# Revit family: TR3106
name_source: partatom
category: Verbindungsmittel
units: mm (PartAtom-declared; Revit-internal decimal feet)

## family parameters
Arbeitsebenenbasiert = Nein
Beim Laden mit Abzugskörper schneiden = Nein
Gemeinsam genutzt = Nein
Immer vertikal = Nein
OmniClass-Nummer = 23.25.10.27.11.21
OmniClass-Titel = Reinforcement Couplers

## types (9) — shared parameters
Endenbearbeitung 1 = Mit Gewinde
Endenbearbeitung 2 = Mit Gewinde
Hersteller = Stahlwerk Annahütte Max Aicher GmbH Co.KG
Körper = 0,00 kg
Modell = TR 3106
TR3106-L_Vis = Ja
TR3106_Vis = Ja
Typenbild = TR3106.png
URL = http//:www.annahuette.com

## per-type parameters (varying)
| type | Außendurchmesser | Beschreibung | Einfassung Stab 1 | Einfassung Stab 2 | Gesamtlänge | Stabgröße 1 | Stabgröße 2 | TR3106-L | TR3106-L0 | TR3106-L1 | TR3106-L2 | TR3106-Stab1 | TR3106-Stab2 | TR3106-ød | Typenkommentare |
| TR 3106-ø22/18 | 32 mm  [stored 0.104987 ft] | TR3106-ø22/18 | 35 mm  [stored 0.114829 ft] | 35 mm  [stored 0.114829 ft] | 90 mm  [stored 0.295276 ft] | SAS 670 - ø22 | SAS 670 - ø18 | 90 mm  [stored 0.295276 ft] | 45 mm  [stored 0.147638 ft] | 35 mm  [stored 0.114829 ft] | 35 mm  [stored 0.114829 ft] | 22 mm  [stored 0.0721785 ft] | 18 mm  [stored 0.0590551 ft] | 32 mm  [stored 0.104987 ft] | TR 3106 - Reduzier-Kontaktmuffe |
| TR 3106-ø25/22 | 40 mm  [stored 0.131234 ft] | TR3106-ø25/22 | 40 mm  [stored 0.131234 ft] | 35 mm  [stored 0.114829 ft] | 95 mm | SAS 670 - ø25 | SAS 670 - ø22 | 95 mm | 48 mm | 40 mm  [stored 0.131234 ft] | 35 mm  [stored 0.114829 ft] | 25 mm  [stored 0.082021 ft] | 22 mm  [stored 0.0721785 ft] | 40 mm  [stored 0.131234 ft] | TR 3106 - Reduzier-Kontaktmuffe |
| TR 3106-ø28/25 | 45 mm  [stored 0.147638 ft] | TR3106-ø28/25 | 45 mm  [stored 0.147638 ft] | 40 mm  [stored 0.131234 ft] | 110 mm  [stored 0.360892 ft] | SAS 670 - ø28 | SAS 670 - ø25 | 110 mm  [stored 0.360892 ft] | 55 mm  [stored 0.180446 ft] | 45 mm  [stored 0.147638 ft] | 40 mm  [stored 0.131234 ft] | 28 mm  [stored 0.0918635 ft] | 25 mm  [stored 0.082021 ft] | 45 mm  [stored 0.147638 ft] | TR 3106 - Reduzier-Kontaktmuffe |
| TR 3106-ø30/28 | 45 mm  [stored 0.147638 ft] | TR3106-ø30/28 | 45 mm  [stored 0.147638 ft] | 45 mm  [stored 0.147638 ft] | 115 mm  [stored 0.377297 ft] | SAS 670 - ø30 | SAS 670 - ø28 | 115 mm  [stored 0.377297 ft] | 58 mm | 45 mm  [stored 0.147638 ft] | 45 mm  [stored 0.147638 ft] | 30 mm  [stored 0.0984252 ft] | 28 mm  [stored 0.0918635 ft] | 45 mm  [stored 0.147638 ft] | TR 3106 - Reduzier-Kontaktmuffe |
| TR 3106-ø35/30 | 50 mm  [stored 0.164042 ft] | TR3106-ø35/30 | 60 mm  [stored 0.19685 ft] | 45 mm  [stored 0.147638 ft] | 135 mm  [stored 0.442913 ft] | SAS 670 - ø35 | SAS 670 - ø30 | 135 mm  [stored 0.442913 ft] | 68 mm | 60 mm  [stored 0.19685 ft] | 45 mm  [stored 0.147638 ft] | 35 mm  [stored 0.114829 ft] | 30 mm  [stored 0.0984252 ft] | 50 mm  [stored 0.164042 ft] | TR 3106 - Rduzier-Kontaktmuffe |
| TR 3106-ø43/35 | 65 mm  [stored 0.213255 ft] | TR3106-ø43/35 | 80 mm  [stored 0.262467 ft] | 60 mm  [stored 0.19685 ft] | 185 mm  [stored 0.606955 ft] | SAS 670 - ø43 | SAS 670 - ø35 | 185 mm  [stored 0.606955 ft] | 93 mm | 80 mm  [stored 0.262467 ft] | 60 mm  [stored 0.19685 ft] | 43 mm  [stored 0.141076 ft] | 35 mm  [stored 0.114829 ft] | 65 mm  [stored 0.213255 ft] | TR 3106 - Reduzier-Kontaktmuffe |
| TR 3106-ø57,5/50 | 81 mm  [stored 0.265748 ft] | TR3106-ø57,5/50 | 90 mm  [stored 0.295276 ft] | 85 mm  [stored 0.278871 ft] | 220 mm  [stored 0.721785 ft] | SAS 670 - ø57,5 | SAS 670 - ø50 | 220 mm  [stored 0.721785 ft] | 110 mm  [stored 0.360892 ft] | 90 mm  [stored 0.295276 ft] | 85 mm  [stored 0.278871 ft] | 58 mm | 50 mm  [stored 0.164042 ft] | 81 mm  [stored 0.265748 ft] | TR 3106 - Reduzier-Kontaktmuffe |
| TR 3106-ø63,5/57,5 | 90 mm  [stored 0.295276 ft] | TR3106-ø63,5/57,5 | 100 mm  [stored 0.328084 ft] | 90 mm  [stored 0.295276 ft] | 245 mm  [stored 0.803806 ft] | SAS 670 - ø63,5 | SAS 670 - ø57,5 | 245 mm  [stored 0.803806 ft] | 123 mm | 100 mm  [stored 0.328084 ft] | 90 mm  [stored 0.295276 ft] | 64 mm | 58 mm | 90 mm  [stored 0.295276 ft] | TR 3106 - Reduzier-Kontaktmuffe |
| TR 3106-ø50/43 | 70 mm  [stored 0.229659 ft] | TR3106-ø50/43 | 85 mm  [stored 0.278871 ft] | 80 mm  [stored 0.262467 ft] | 210 mm  [stored 0.688976 ft] | SAS 670 - ø50 | SAS 670 - ø43 | 210 mm  [stored 0.688976 ft] | 105 mm  [stored 0.344488 ft] | 85 mm  [stored 0.278871 ft] | 80 mm  [stored 0.262467 ft] | 50 mm  [stored 0.164042 ft] | 43 mm  [stored 0.141076 ft] | 70 mm  [stored 0.229659 ft] | TR 3106 - Reduzier-Kontaktmuffe |

note: [stored X ft] marks values corroborated as IEEE doubles in the binary element streams (Revit-internal decimal feet)
